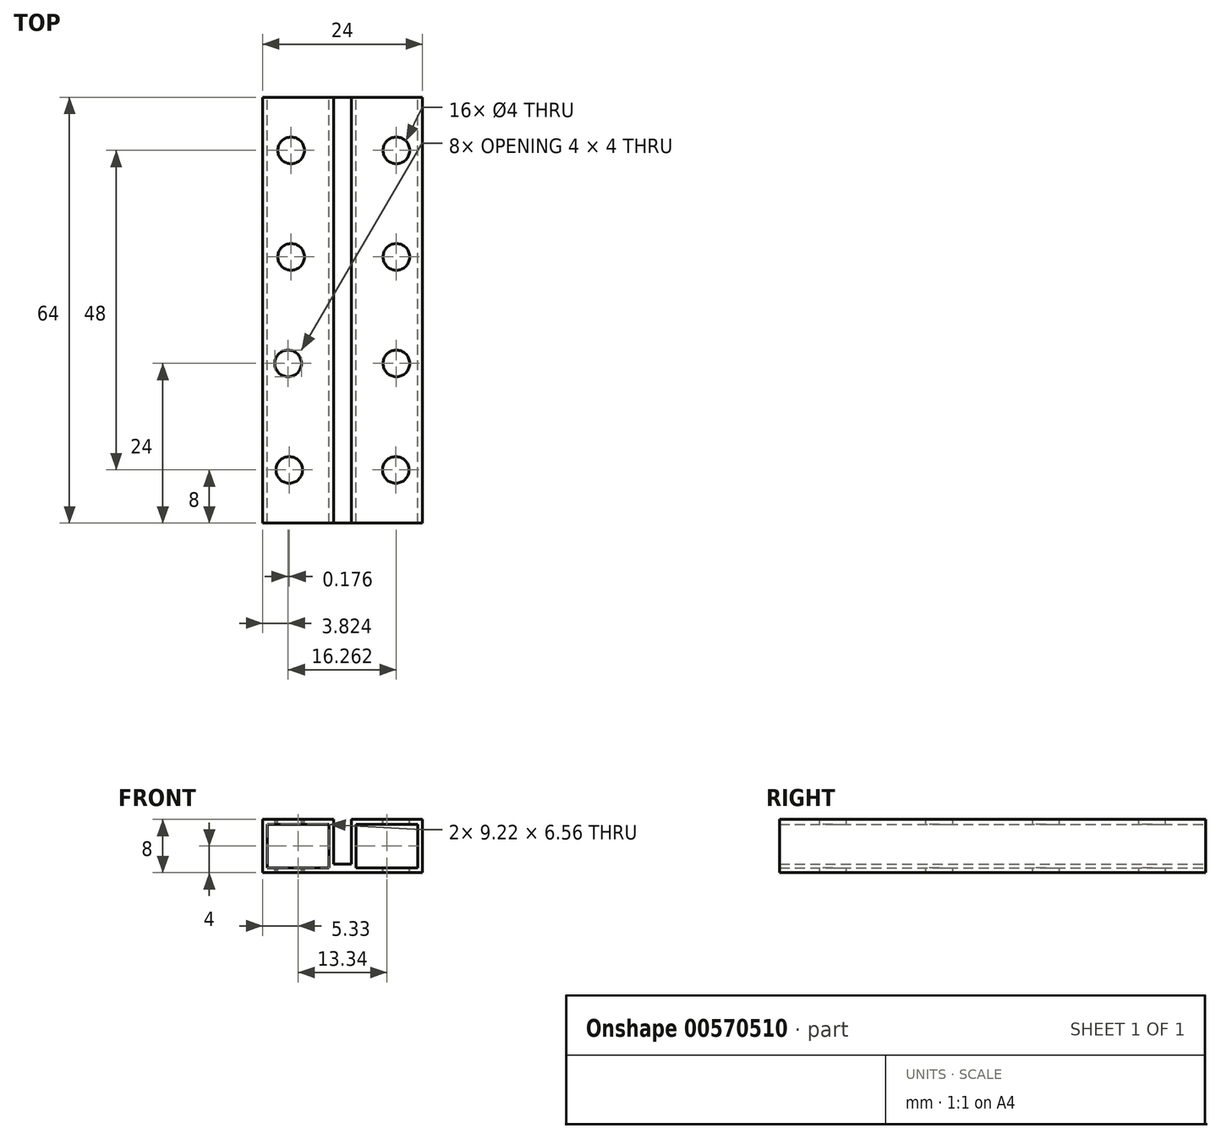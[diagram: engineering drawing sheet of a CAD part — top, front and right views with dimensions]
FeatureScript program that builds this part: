
annotation { "Feature Type Name" : "Feature", "Feature Type Description" : "" }
export const myFeature = defineFeature(function(context is Context, id is Id, definition is map)
    precondition{}
    {
        {
            var Q0;
            Q0=qCreatedBy(makeId("Front.planeOp"),FACE);
            var sketch = newSketch(context, id + "F0", { "sketchPlane" : qUnion([Q0])});
            skLineSegment(sketch, "E0.bottom", {"start": v(-12, 4) * mm, "end": v(12, 4) * mm});
            skLineSegment(sketch, "E0.top", {"start": v(-12, -4) * mm, "end": v(12, -4) * mm});
            skLineSegment(sketch, "E0.left", {"start": v(-12, 4) * mm, "end": v(-12, -4) * mm});
            skLineSegment(sketch, "E0.right", {"start": v(12, 4) * mm, "end": v(12, -4) * mm});
            skPoint(sketch, "E0.middle", {"position": v(0, 0) * mm});
            skLineSegment(sketch, "E1.bottom", {"start": v(-1.34, 10.75) * mm, "end": v(1.34, 10.75) * mm});
            skLineSegment(sketch, "E1.top", {"start": v(-1.34, -2.75) * mm, "end": v(1.34, -2.75) * mm});
            skLineSegment(sketch, "E1.left", {"start": v(-1.34, 10.75) * mm, "end": v(-1.34, -2.75) * mm});
            skLineSegment(sketch, "E1.right", {"start": v(1.34, 10.75) * mm, "end": v(1.34, -2.75) * mm});
            skPoint(sketch, "E1.middle", {"position": v(0, 4) * mm});
            skLineSegment(sketch, "E2.bottom", {"start": v(11.28, -3.28) * mm, "end": v(2.06, -3.28) * mm});
            skLineSegment(sketch, "E2.top", {"start": v(11.28, 3.28) * mm, "end": v(2.06, 3.28) * mm});
            skLineSegment(sketch, "E2.left", {"start": v(11.28, -3.28) * mm, "end": v(11.28, 3.28) * mm});
            skLineSegment(sketch, "E2.right", {"start": v(2.06, -3.28) * mm, "end": v(2.06, 3.28) * mm});
            skLineSegment(sketch, "E3.bottom", {"start": v(-2.06, 3.28) * mm, "end": v(-11.28, 3.28) * mm});
            skLineSegment(sketch, "E3.top", {"start": v(-2.06, -3.28) * mm, "end": v(-11.28, -3.28) * mm});
            skLineSegment(sketch, "E3.left", {"start": v(-2.06, 3.28) * mm, "end": v(-2.06, -3.28) * mm});
            skLineSegment(sketch, "E3.right", {"start": v(-11.28, 3.28) * mm, "end": v(-11.28, -3.28) * mm});
            skLineSegment(sketch, "E4.bottom", {"start": v(-9.78, 3.28) * mm, "end": v(-6.31, 3.28) * mm});
            skLineSegment(sketch, "E4.top", {"start": v(-9.78, -3.28) * mm, "end": v(-6.31, -3.28) * mm});
            skLineSegment(sketch, "E4.left", {"start": v(-9.78, 3.28) * mm, "end": v(-9.78, -3.28) * mm});
            skLineSegment(sketch, "E4.right", {"start": v(-6.31, 3.28) * mm, "end": v(-6.31, -3.28) * mm});
            skLineSegment(sketch, "E5.bottom", {"start": v(6.31, 3.28) * mm, "end": v(9.78, 3.28) * mm});
            skLineSegment(sketch, "E5.top", {"start": v(6.31, -3.28) * mm, "end": v(9.78, -3.28) * mm});
            skLineSegment(sketch, "E5.left", {"start": v(6.31, 3.28) * mm, "end": v(6.31, -3.28) * mm});
            skLineSegment(sketch, "E5.right", {"start": v(9.78, 3.28) * mm, "end": v(9.78, -3.28) * mm});
            skCircle(sketch, "E6", {"center": v(-8, 0) * mm, "radius": 2.16 * mm});
            skCircle(sketch, "E7", {"center": v(8, 0) * mm, "radius": 2.16 * mm});
            skSolve(sketch);
        }
        {
            var Q0;
            Q0=makeQuery(id+"F0.imprint","IMPRINT",FACE,{"disambiguationData":[TD([[makeQuery(id+"F0.imprint","IMPRINT",EDGE,{"derivedFrom":sQuery(id+"F0.wireOp",EDGE,"E0.top")}),1.0]])]});
            var Q1;
            {var subQ0=sQuery(id+"F0.wireOp",EDGE,"E4.bottom");Q1=makeQuery(id+"F0.imprint","IMPRINT",FACE,{"disambiguationData":[TD([[makeQuery(id+"F0.imprint","IMPRINT",EDGE,{"derivedFrom":subQ0}),-1.0]])]});}
            var Q2;
            {var subQ0=sQuery(id+"F0.wireOp",EDGE,"E4.top");Q2=makeQuery(id+"F0.imprint","IMPRINT",FACE,{"disambiguationData":[TD([[makeQuery(id+"F0.imprint","IMPRINT",EDGE,{"derivedFrom":subQ0}),1.0]])]});}
            var Q3;
            {var subQ0=sQuery(id+"F0.wireOp",EDGE,"E5.bottom");Q3=makeQuery(id+"F0.imprint","IMPRINT",FACE,{"disambiguationData":[TD([[makeQuery(id+"F0.imprint","IMPRINT",EDGE,{"derivedFrom":subQ0}),-1.0]])]});}
            var Q4;
            {var subQ0=sQuery(id+"F0.wireOp",EDGE,"E5.top");Q4=makeQuery(id+"F0.imprint","IMPRINT",FACE,{"disambiguationData":[TD([[makeQuery(id+"F0.imprint","IMPRINT",EDGE,{"derivedFrom":subQ0}),1.0]])]});}
            extrude(context, id + "F1", {"entities" : qUnion([Q0, Q1, Q2, Q3, Q4]), "depth" : 64 * mm, "offsetDistance" : 25 * mm});
        }
        {
            var Q0;
            {var subQ0=sQuery(id+"F0.wireOp",EDGE,"E0.bottom");Q0=makeQuery(id+"F1.opExtrude","SWEPT_FACE",FACE,{"disambiguationData":[OSD([subQ0]),TDD([makeQuery(id+"F0.imprint","IMPRINT",EDGE,{"disambiguationData":[TD([[makeQuery(id+"F0.imprint","INTERSECT",VERTEX,{"derivedFrom":[subQ0,sQuery(id+"F0.wireOp",EDGE,"E0.right")]}),1.0]])],"derivedFrom":subQ0})])]});}
            var sketch = newSketch(context, id + "F2", { "sketchPlane" : qUnion([Q0])});
            skCircle(sketch, "E8", {"center": v(8, -56) * mm, "radius": 2 * mm});
            skCircle(sketch, "E9", {"center": v(-8, -56) * mm, "radius": 2 * mm});
            skCircle(sketch, "E10", {"center": v(8.09, -40) * mm, "radius": 2 * mm});
            skCircle(sketch, "E11", {"center": v(-8.18, -40) * mm, "radius": 2 * mm});
            skCircle(sketch, "E12", {"center": v(8.09, -24) * mm, "radius": 2 * mm});
            skCircle(sketch, "E13", {"center": v(-7.73, -24) * mm, "radius": 2 * mm});
            skCircle(sketch, "E14", {"center": v(8.09, -8) * mm, "radius": 2 * mm});
            skCircle(sketch, "E15", {"center": v(-7.73, -8) * mm, "radius": 2 * mm});
            skSolve(sketch);
        }
        {
            var Q0;
            Q0=makeQuery(id+"F2.imprint","IMPRINT",FACE,{"disambiguationData":[TD([[makeQuery(id+"F2.imprint","IMPRINT",EDGE,{"derivedFrom":sQuery(id+"F2.wireOp",EDGE,"E9")}),1.0]])]});
            var Q1;
            Q1=makeQuery(id+"F2.imprint","IMPRINT",FACE,{"disambiguationData":[TD([[makeQuery(id+"F2.imprint","IMPRINT",EDGE,{"derivedFrom":sQuery(id+"F2.wireOp",EDGE,"E8")}),1.0]])]});
            var Q2;
            Q2=makeQuery(id+"F2.imprint","IMPRINT",FACE,{"disambiguationData":[TD([[makeQuery(id+"F2.imprint","IMPRINT",EDGE,{"derivedFrom":sQuery(id+"F2.wireOp",EDGE,"E11")}),1.0]])]});
            var Q3;
            Q3=makeQuery(id+"F2.imprint","IMPRINT",FACE,{"disambiguationData":[TD([[makeQuery(id+"F2.imprint","IMPRINT",EDGE,{"derivedFrom":sQuery(id+"F2.wireOp",EDGE,"E10")}),1.0]])]});
            var Q4;
            Q4=makeQuery(id+"F2.imprint","IMPRINT",FACE,{"disambiguationData":[TD([[makeQuery(id+"F2.imprint","IMPRINT",EDGE,{"derivedFrom":sQuery(id+"F2.wireOp",EDGE,"E13")}),1.0]])]});
            var Q5;
            Q5=makeQuery(id+"F2.imprint","IMPRINT",FACE,{"disambiguationData":[TD([[makeQuery(id+"F2.imprint","IMPRINT",EDGE,{"derivedFrom":sQuery(id+"F2.wireOp",EDGE,"E12")}),1.0]])]});
            var Q6;
            Q6=makeQuery(id+"F2.imprint","IMPRINT",FACE,{"disambiguationData":[TD([[makeQuery(id+"F2.imprint","IMPRINT",EDGE,{"derivedFrom":sQuery(id+"F2.wireOp",EDGE,"E15")}),1.0]])]});
            var Q7;
            Q7=makeQuery(id+"F2.imprint","IMPRINT",FACE,{"disambiguationData":[TD([[makeQuery(id+"F2.imprint","IMPRINT",EDGE,{"derivedFrom":sQuery(id+"F2.wireOp",EDGE,"E14")}),1.0]])]});
            extrude(context, id + "F3", {"entities" : qUnion([Q0, Q1, Q2, Q3, Q4, Q5, Q6, Q7]), "operationType" : NewBodyOperationType.REMOVE, "oppositeDirection" : true, "depth" : 8.1 * mm, "offsetDistance" : 25 * mm});
        }
    });
